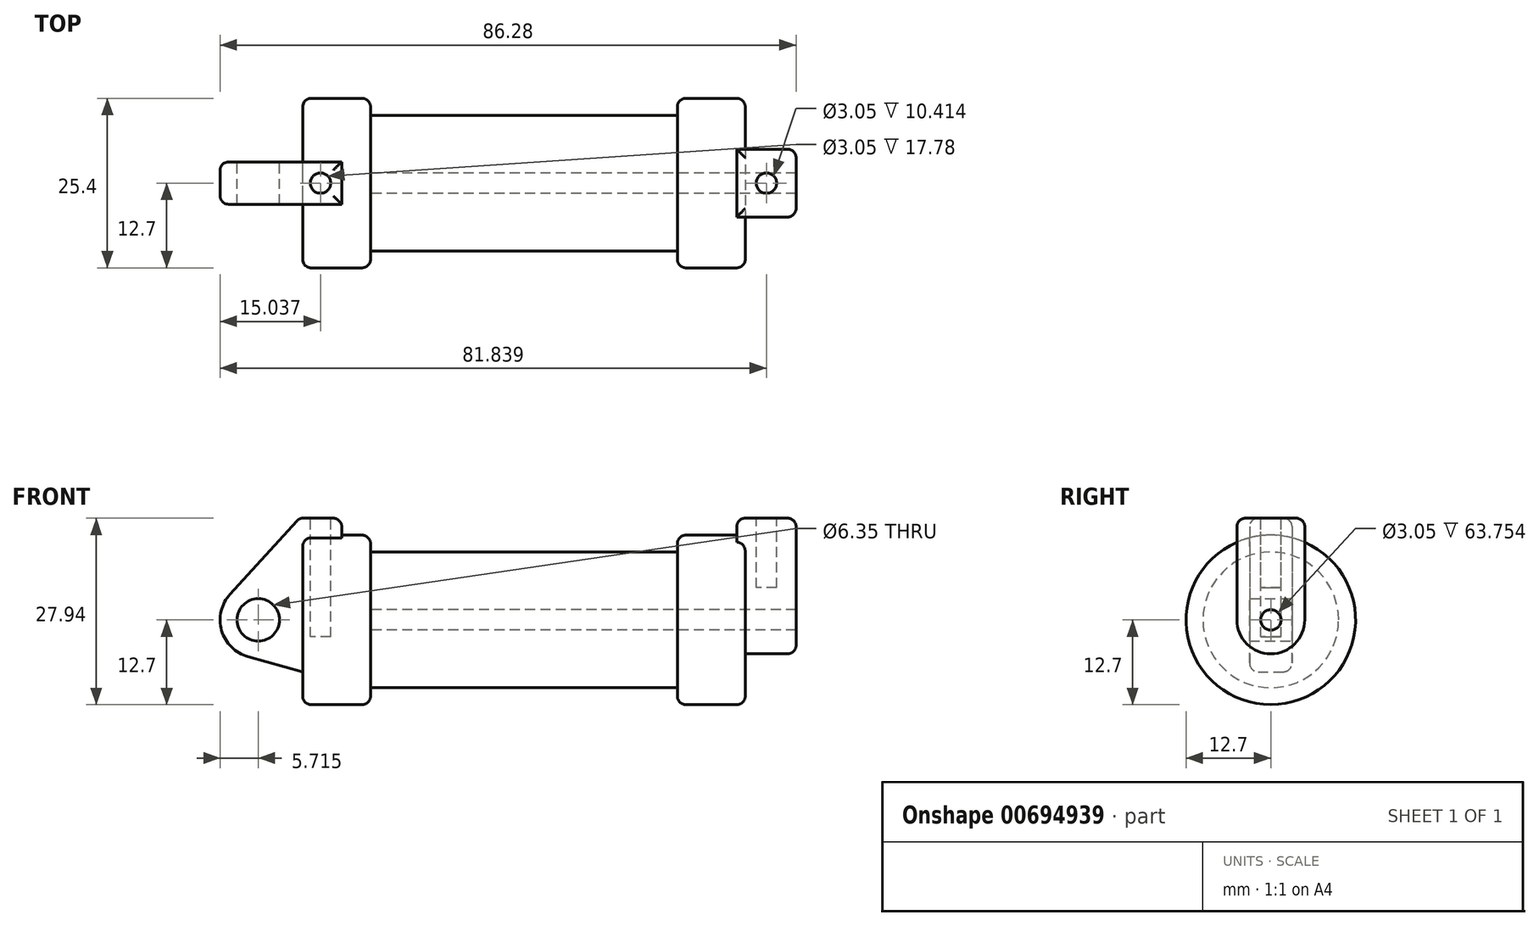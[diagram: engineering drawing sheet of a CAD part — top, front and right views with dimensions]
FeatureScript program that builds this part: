
annotation { "Feature Type Name" : "Feature", "Feature Type Description" : "" }
export const myFeature = defineFeature(function(context is Context, id is Id, definition is map)
    precondition{}
    {
        {
            var Q0;
            Q0=qCreatedBy(makeId("Front.planeOp"),FACE);
            var sketch = newSketch(context, id + "F0", { "sketchPlane" : qUnion([Q0])});
            skLineSegment(sketch, "E0", {"start": v(0, 0) * mm, "end": v(0, 12.7) * mm});
            skLineSegment(sketch, "E1", {"start": v(0, 12.7) * mm, "end": v(10.16, 12.7) * mm});
            skLineSegment(sketch, "E2", {"start": v(10.16, 12.7) * mm, "end": v(10.16, 10.16) * mm});
            skLineSegment(sketch, "E3", {"start": v(10.16, 10.16) * mm, "end": v(56.13, 10.16) * mm});
            skLineSegment(sketch, "E4", {"start": v(56.13, 10.16) * mm, "end": v(56.13, 12.7) * mm});
            skLineSegment(sketch, "E5", {"start": v(56.13, 12.7) * mm, "end": v(66.3, 12.7) * mm});
            skLineSegment(sketch, "E6", {"start": v(66.3, 12.7) * mm, "end": v(66.3, 0) * mm});
            skLineSegment(sketch, "E7", {"start": v(66.3, 0) * mm, "end": v(0, 0) * mm});
            skLineSegment(sketch, "E8", {"start": v(5.84, 15.24) * mm, "end": v(-0.5, 15.24) * mm});
            skLineSegment(sketch, "E9", {"start": v(-0.5, 15.24) * mm, "end": v(-10.88, 3.85) * mm});
            skLineSegment(sketch, "E10", {"start": v(0, 0) * mm, "end": v(-6.65, 0) * mm});
            skCircle(sketch, "E11", {"center": v(-6.65, 0) * mm, "radius": 5.72 * mm});
            skCircle(sketch, "E12", {"center": v(-6.65, 0) * mm, "radius": 3.18 * mm});
            skLineSegment(sketch, "E13", {"start": v(5.84, 15.24) * mm, "end": v(5.84, -9.4) * mm});
            skLineSegment(sketch, "E14", {"start": v(5.84, -9.4) * mm, "end": v(-8.18, -5.5) * mm});
            skSolve(sketch);
        }
        {
            var Q0;
            {var subQ0=sQuery(id+"F0.wireOp",EDGE,"E0");Q0=makeQuery(id+"F0.imprint","IMPRINT",FACE,{"disambiguationData":[TD([[makeQuery(id+"F0.imprint","IMPRINT",EDGE,{"derivedFrom":subQ0}),-1.0]])]});}
            var Q1;
            {var subQ0=sQuery(id+"F0.wireOp",EDGE,"E2");Q1=makeQuery(id+"F0.imprint","IMPRINT",FACE,{"disambiguationData":[TD([[makeQuery(id+"F0.imprint","IMPRINT",EDGE,{"derivedFrom":subQ0}),-1.0]])]});}
            var Q2;
            Q2=sQuery(id+"F0.wireOp",EDGE,"E7");
            revolve(context, id + "F1", {"surfaceOperationType" : NewSurfaceOperationType.NEW, "entities" : qUnion([Q0, Q1]), "axis" : qUnion([Q2]), "revolveType" : RevolveType.FULL});
        }
        {
            var Q0;
            {var subQ1=sQuery(id+"F0.wireOp",EDGE,"E0");Q0=makeQuery(id+"F0.imprint","IMPRINT",FACE,{"disambiguationData":[TD([[makeQuery(id+"F0.imprint","IMPRINT",EDGE,{"derivedFrom":subQ1}),1.0]])]});}
            var Q1;
            {var subQ5=sQuery(id+"F0.wireOp",EDGE,"E12");Q1=makeQuery(id+"F0.imprint","IMPRINT",FACE,{"disambiguationData":[TD([[makeQuery(id+"F0.imprint","IMPRINT",EDGE,{"derivedFrom":subQ5}),-1.0]])]});}
            var Q2;
            {var subQ0=sQuery(id+"F0.wireOp",EDGE,"E14");Q2=makeQuery(id+"F0.imprint","IMPRINT",FACE,{"disambiguationData":[TD([[makeQuery(id+"F0.imprint","IMPRINT",EDGE,{"derivedFrom":subQ0}),-1.0]])]});}
            var Q3;
            {var subQ0=sQuery(id+"F0.wireOp",EDGE,"E0");Q3=makeQuery(id+"F0.imprint","IMPRINT",FACE,{"disambiguationData":[TD([[makeQuery(id+"F0.imprint","IMPRINT",EDGE,{"derivedFrom":subQ0}),-1.0]])]});}
            extrude(context, id + "F2", {"entities" : qUnion([Q0, Q1, Q2, Q3]), "operationType" : NewBodyOperationType.ADD, "depth" : 6.35 * mm, "offsetDistance" : 25.4 * mm, "symmetric" : true});
        }
        {
            var Q0;
            Q0=makeQuery(id+"F1.opRevolve","SWEPT_FACE",FACE,{"disambiguationData":[OSD([sQuery(id+"F0.wireOp",EDGE,"E6")])]});
            var sketch = newSketch(context, id + "F3", { "sketchPlane" : qUnion([Q0])});
            skCircle(sketch, "E15", {"center": v(0, 0) * mm, "radius": 5.08 * mm});
            skCircle(sketch, "E16", {"center": v(0, 0) * mm, "radius": 1.52 * mm});
            skLineSegment(sketch, "E17", {"start": v(-5.08, 0) * mm, "end": v(-5.08, 15.24) * mm});
            skLineSegment(sketch, "E18", {"start": v(-5.08, 15.24) * mm, "end": v(0, 15.24) * mm});
            skLineSegment(sketch, "E19", {"start": v(0, 15.24) * mm, "end": v(5.08, 15.24) * mm});
            skLineSegment(sketch, "E20", {"start": v(5.08, 15.24) * mm, "end": v(5.08, 0) * mm});
            skSolve(sketch);
        }
        {
            var Q0;
            Q0 = qSketchRegion(id + "F3", true);
            extrude(context, id + "F4", {"entities" : qUnion([Q0]), "operationType" : NewBodyOperationType.ADD, "depth" : 7.62 * mm, "offsetDistance" : 25.4 * mm, "hasSecondDirection" : true, "secondDirectionOppositeDirection" : true, "secondDirectionDepth" : 1.27 * mm});
        }
        {
            var Q0;
            Q0=makeQuery(id+"F4.boolean.opBoolean","SPLIT",FACE,{"disambiguationData":[TD([makeQuery(id+"F4.opExtrude","SWEPT_FACE",FACE,{"disambiguationData":[OSD([sQuery(id+"F3.wireOp",EDGE,"E16")])]})])],"derivedFrom":makeQuery(id+"F1.opRevolve","SWEPT_FACE",FACE,{"disambiguationData":[OSD([sQuery(id+"F0.wireOp",EDGE,"E6")])]})});
            var Q1;
            Q1=makeQuery(id+"F1.opRevolve","SWEPT_FACE",FACE,{"disambiguationData":[OSD([sQuery(id+"F0.wireOp",EDGE,"E2")])]});
            extrude(context, id + "F5", {"entities" : qUnion([Q0]), "operationType" : NewBodyOperationType.REMOVE, "endBound" : BoundingType.UP_TO_SURFACE, "oppositeDirection" : true, "depth" : 25.4 * mm, "endBoundEntityFace" : qUnion([Q1]), "offsetDistance" : 25.4 * mm});
        }
        {
            var Q0;
            Q0=makeQuery(id+"F2.opExtrude","SWEPT_FACE",FACE,{"disambiguationData":[OSD([sQuery(id+"F0.wireOp",EDGE,"E8")])]});
            var sketch = newSketch(context, id + "F6", { "sketchPlane" : qUnion([Q0])});
            skLineSegment(sketch, "E21", {"start": v(2.67, 3.18) * mm, "end": v(2.67, -3.18) * mm, "construction": true});
            skLineSegment(sketch, "E22", {"start": v(-0.5, 0) * mm, "end": v(5.84, 0) * mm, "construction": true});
            skCircle(sketch, "E23", {"center": v(2.67, 0) * mm, "radius": 1.52 * mm});
            skSolve(sketch);
        }
        {
            var Q0;
            Q0=makeQuery(id+"F4.opExtrude","SWEPT_FACE",FACE,{"disambiguationData":[OSD([sQuery(id+"F3.wireOp",EDGE,"E18"),sQuery(id+"F3.wireOp",EDGE,"E19")])]});
            var sketch = newSketch(context, id + "F7", { "sketchPlane" : qUnion([Q0])});
            skLineSegment(sketch, "E24", {"start": v(65.02, 0) * mm, "end": v(73.91, 0) * mm, "construction": true});
            skLineSegment(sketch, "E25", {"start": v(69.47, -5.08) * mm, "end": v(69.47, 5.08) * mm, "construction": true});
            skCircle(sketch, "E26", {"center": v(69.47, 0) * mm, "radius": 1.52 * mm});
            skSolve(sketch);
        }
        {
            var Q0;
            Q0=makeQuery(id+"F7.imprint","IMPRINT",FACE,{"disambiguationData":[TD([[makeQuery(id+"F7.imprint","IMPRINT",EDGE,{"derivedFrom":sQuery(id+"F7.wireOp",EDGE,"E26")}),1.0]])]});
            extrude(context, id + "F8", {"entities" : qUnion([Q0]), "operationType" : NewBodyOperationType.REMOVE, "oppositeDirection" : true, "depth" : 10.4 * mm, "offsetDistance" : 25.4 * mm});
        }
        {
            var Q0;
            Q0=makeQuery(id+"F6.imprint","IMPRINT",FACE,{"disambiguationData":[TD([[makeQuery(id+"F6.imprint","IMPRINT",EDGE,{"derivedFrom":sQuery(id+"F6.wireOp",EDGE,"E23")}),1.0]])]});
            extrude(context, id + "F9", {"entities" : qUnion([Q0]), "operationType" : NewBodyOperationType.REMOVE, "oppositeDirection" : true, "depth" : 17.78 * mm, "offsetDistance" : 25.4 * mm});
        }
        {
            var Q0;
            Q0=makeQuery(id+"F1.opRevolve","SWEPT_EDGE",EDGE,{"disambiguationData":[OSD([sQuery(id+"F0.wireOp",EDGE,"E1"),sQuery(id+"F0.wireOp",EDGE,"E2")])]});
            var Q1;
            Q1=makeQuery(id+"F1.opRevolve","SWEPT_EDGE",EDGE,{"disambiguationData":[OSD([sQuery(id+"F0.wireOp",EDGE,"E4"),sQuery(id+"F0.wireOp",EDGE,"E5")])]});
            var Q2;
            Q2=makeQuery(id+"F1.opRevolve","SWEPT_EDGE",EDGE,{"disambiguationData":[OSD([sQuery(id+"F0.wireOp",EDGE,"E0"),sQuery(id+"F0.wireOp",EDGE,"E1")])]});
            var Q3;
            Q3=makeQuery(id+"F1.opRevolve","SWEPT_EDGE",EDGE,{"disambiguationData":[OSD([sQuery(id+"F0.wireOp",EDGE,"E5"),sQuery(id+"F0.wireOp",EDGE,"E6")])]});
            var Q4;
            Q4=makeQuery(id+"F2.opExtrude","CAP_EDGE",EDGE,{"disambiguationData":[OSD([sQuery(id+"F0.wireOp",EDGE,"E8")])],"isStart":false});
            var Q5;
            Q5=makeQuery(id+"F2.opExtrude","CAP_EDGE",EDGE,{"disambiguationData":[OSD([sQuery(id+"F0.wireOp",EDGE,"E8")])],"isStart":true});
            var Q6;
            Q6=makeQuery(id+"F2.opExtrude","SWEPT_EDGE",EDGE,{"disambiguationData":[OSD([sQuery(id+"F0.wireOp",EDGE,"E8"),sQuery(id+"F0.wireOp",EDGE,"E13")])]});
            var Q7;
            Q7=makeQuery(id+"F2.opExtrude","SWEPT_EDGE",EDGE,{"disambiguationData":[OSD([sQuery(id+"F0.wireOp",EDGE,"E8"),sQuery(id+"F0.wireOp",EDGE,"E9")])]});
            var Q8;
            Q8=makeQuery(id+"F4.opExtrude","CAP_EDGE",EDGE,{"disambiguationData":[OSD([sQuery(id+"F3.wireOp",EDGE,"E18"),sQuery(id+"F3.wireOp",EDGE,"E19")])],"isStart":false});
            var Q9;
            Q9=makeQuery(id+"F4.opExtrude","SWEPT_EDGE",EDGE,{"disambiguationData":[OSD([sQuery(id+"F3.wireOp",EDGE,"E17"),sQuery(id+"F3.wireOp",EDGE,"E18")])]});
            var Q10;
            Q10=makeQuery(id+"F4.opExtrude","CAP_EDGE",EDGE,{"disambiguationData":[OSD([sQuery(id+"F3.wireOp",EDGE,"E18"),sQuery(id+"F3.wireOp",EDGE,"E19")])],"isStart":true});
            var Q11;
            Q11=makeQuery(id+"F4.opExtrude","SWEPT_EDGE",EDGE,{"disambiguationData":[OSD([sQuery(id+"F3.wireOp",EDGE,"E19"),sQuery(id+"F3.wireOp",EDGE,"E20")])]});
            var Q12;
            Q12=makeQuery(id+"F4.opExtrude","CAP_EDGE",EDGE,{"disambiguationData":[OSD([sQuery(id+"F3.wireOp",EDGE,"E17")])],"isStart":false});
            var Q13;
            Q13=makeQuery(id+"F4.opExtrude","CAP_EDGE",EDGE,{"disambiguationData":[OSD([sQuery(id+"F3.wireOp",EDGE,"E20")])],"isStart":false});
            var Q14;
            Q14=makeQuery(id+"F2.opExtrude","CAP_EDGE",EDGE,{"disambiguationData":[OSD([sQuery(id+"F0.wireOp",EDGE,"E9")])],"isStart":false});
            var Q15;
            Q15=makeQuery(id+"F2.opExtrude","CAP_EDGE",EDGE,{"disambiguationData":[OSD([sQuery(id+"F0.wireOp",EDGE,"E9")])],"isStart":true});
            fillet(context, id + "F10", {"entities" : qUnion([Q0, Q1, Q2, Q3, Q4, Q5, Q6, Q7, Q8, Q9, Q10, Q11, Q12, Q13, Q14, Q15]), "radius" : 1.27 * mm, "tangentPropagation" : true, "allowEdgeOverflow" : false});
        }
    });
